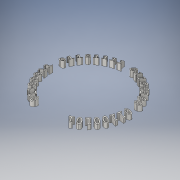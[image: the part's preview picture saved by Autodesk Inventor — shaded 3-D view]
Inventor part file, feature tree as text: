
AUTODESK INVENTOR PART (.ipt)
format: ipt  version: 2016 (Build 200138000, 138)  size: 1,372,672 bytes
history: native  units: in
note: dims shown in document units (in); Inventor stores cm internally (conversion verified against a paired STEP export)
features: sketch x2, revolve x1, extrude x1, projected_geometry x1
ambient origin geometry x8: Origin, YZ Plane, XZ Plane, XY Plane, X Axis, Y Axis, Z Axis, Center Point
bodies: Solid1 (feature_tree)
feature tree (5):
  revolve  "Revolution1"  [1 undecoded]
  extrude  "Extrusion1"  Depth=0.1in
  sketch  "Sketch1"  dims[d0=0.8265in d1=0.175in]
  sketch  "Sketch2"  dims[d2=0.05in d3=0.1in d4=0.15in d5=0.275in d6=90.0deg d7=0.075in d8=1.0in d9=0.0in]
  projected_geometry  "Projected Loop1"
note: 1 required parameter value undecoded (feature->parameter linkage not recoverable at this tier; creation-order binding heuristic only, values carry confidence <= 0.55)
